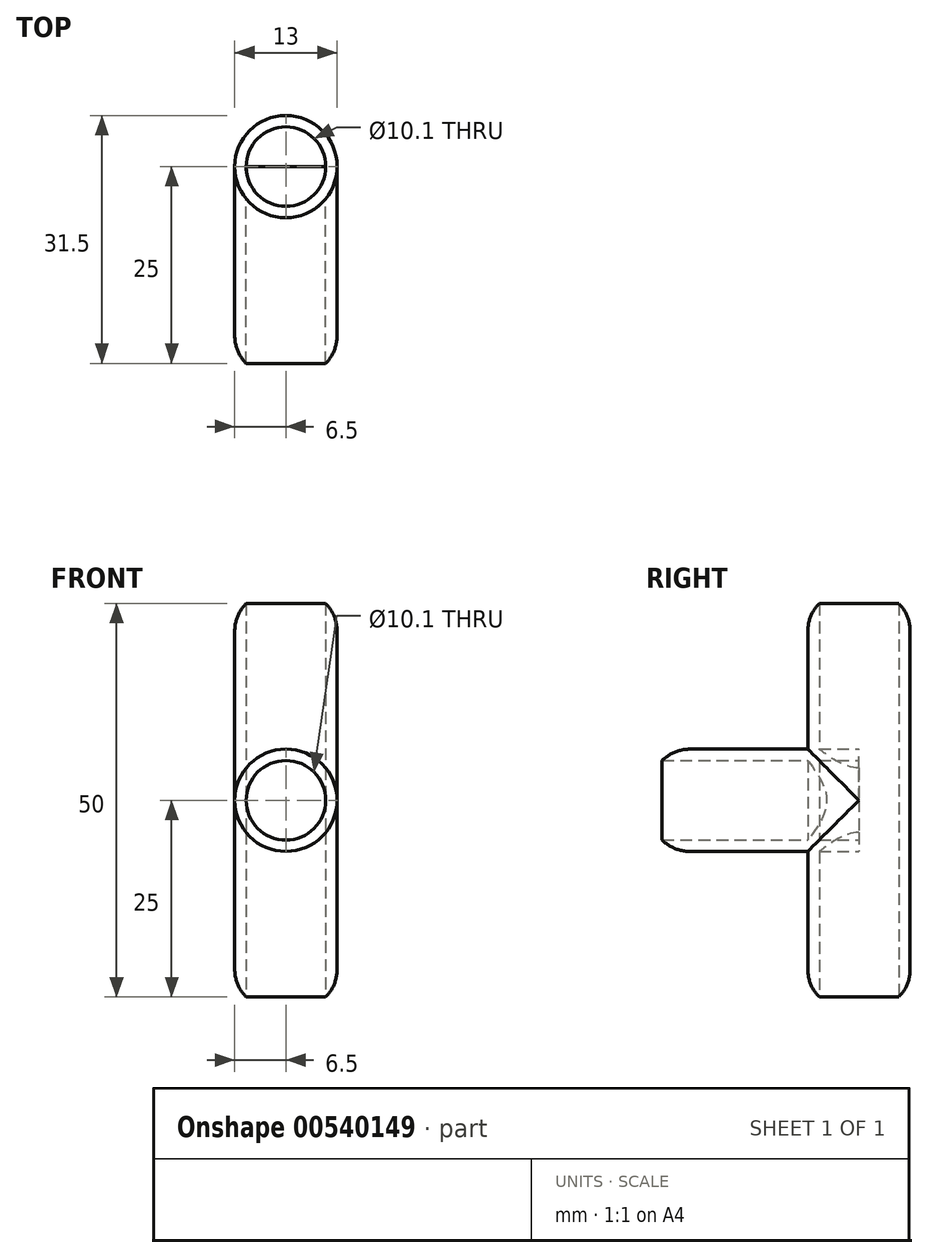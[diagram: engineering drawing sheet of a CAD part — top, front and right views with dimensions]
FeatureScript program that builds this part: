
annotation { "Feature Type Name" : "Feature", "Feature Type Description" : "" }
export const myFeature = defineFeature(function(context is Context, id is Id, definition is map)
    precondition{}
    {
        {
            var Q0;
            Q0=qCreatedBy(makeId("Top.planeOp"),FACE);
            var sketch = newSketch(context, id + "F0", { "sketchPlane" : qUnion([Q0])});
            skCircle(sketch, "E0", {"center": v(0, 0) * mm, "radius": 6.5 * mm});
            skCircle(sketch, "E1", {"center": v(0, 0) * mm, "radius": 5.05 * mm});
            skSolve(sketch);
        }
        {
            var Q0;
            Q0=makeQuery(id+"F0.imprint","IMPRINT",FACE,{"disambiguationData":[TD([[makeQuery(id+"F0.imprint","IMPRINT",EDGE,{"derivedFrom":sQuery(id+"F0.wireOp",EDGE,"E0")}),1.0]])]});
            extrude(context, id + "F1", {"entities" : qUnion([Q0]), "depth" : 25 * mm, "offsetDistance" : 25 * mm});
        }
        {
            var Q0;
            Q0=makeQuery(id+"F0.imprint","IMPRINT",FACE,{"disambiguationData":[TD([[makeQuery(id+"F0.imprint","IMPRINT",EDGE,{"derivedFrom":sQuery(id+"F0.wireOp",EDGE,"E0")}),1.0]])]});
            extrude(context, id + "F2", {"entities" : qUnion([Q0]), "operationType" : NewBodyOperationType.ADD, "oppositeDirection" : true, "depth" : 25 * mm, "offsetDistance" : 25 * mm});
        }
        {
            var Q0;
            Q0=qCreatedBy(makeId("Front.planeOp"),FACE);
            var sketch = newSketch(context, id + "F3", { "sketchPlane" : qUnion([Q0])});
            skCircle(sketch, "E2", {"center": v(0, 0) * mm, "radius": 6.5 * mm});
            skCircle(sketch, "E3", {"center": v(0, 0) * mm, "radius": 5.05 * mm});
            skSolve(sketch);
        }
        {
            var Q0;
            Q0=makeQuery(id+"F3.imprint","IMPRINT",FACE,{"disambiguationData":[TD([[makeQuery(id+"F3.imprint","IMPRINT",EDGE,{"derivedFrom":sQuery(id+"F3.wireOp",EDGE,"E2")}),1.0]])]});
            extrude(context, id + "F4", {"entities" : qUnion([Q0]), "operationType" : NewBodyOperationType.ADD, "depth" : 25 * mm, "offsetDistance" : 25 * mm});
        }
        {
            var Q0;
            Q0=makeQuery(id+"F4.opExtrude","CAP_EDGE",EDGE,{"disambiguationData":[OSD([sQuery(id+"F3.wireOp",EDGE,"E2")])],"isStart":false});
            var Q1;
            Q1=makeQuery(id+"F2.opExtrude","CAP_EDGE",EDGE,{"disambiguationData":[OSD([sQuery(id+"F0.wireOp",EDGE,"E0")])],"isStart":false});
            var Q2;
            Q2=makeQuery(id+"F1.opExtrude","CAP_EDGE",EDGE,{"disambiguationData":[OSD([sQuery(id+"F0.wireOp",EDGE,"E0")])],"isStart":false});
            fillet(context, id + "F5", {"entities" : qUnion([Q0, Q1, Q2]), "radius" : 5 * mm, "tangentPropagation" : true, "allowEdgeOverflow" : false});
        }
    });
